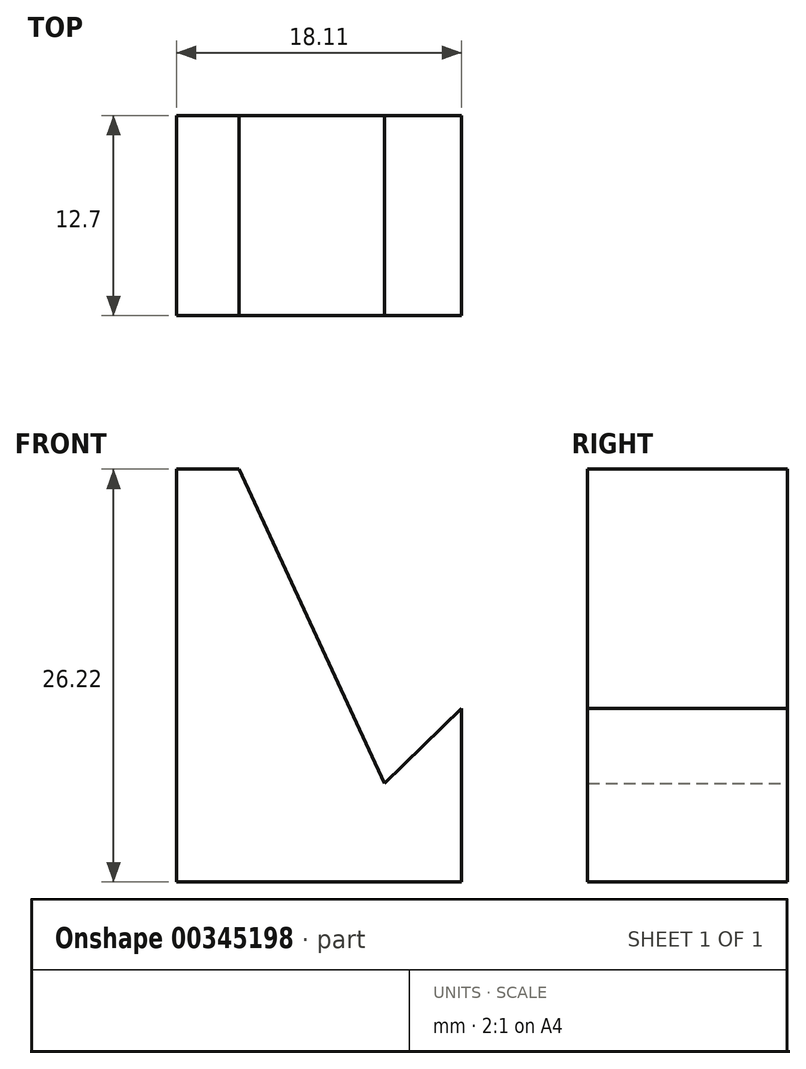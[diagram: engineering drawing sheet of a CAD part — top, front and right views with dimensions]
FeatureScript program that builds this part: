
annotation { "Feature Type Name" : "Feature", "Feature Type Description" : "" }
export const myFeature = defineFeature(function(context is Context, id is Id, definition is map)
    precondition{}
    {
        {
            var Q0;
            Q0=qCreatedBy(makeId("Front.planeOp"),FACE);
            var sketch = newSketch(context, id + "F0", { "sketchPlane" : qUnion([Q0])});
            skLineSegment(sketch, "E0", {"start": v(0, 0) * mm, "end": v(-3.97, 0) * mm});
            skLineSegment(sketch, "E1", {"start": v(-3.97, 0) * mm, "end": v(-3.97, -26.22) * mm});
            skLineSegment(sketch, "E2", {"start": v(-3.97, -26.22) * mm, "end": v(14.14, -26.22) * mm});
            skLineSegment(sketch, "E3", {"start": v(14.14, -26.22) * mm, "end": v(14.14, -15.22) * mm});
            skLineSegment(sketch, "E4", {"start": v(14.14, -15.22) * mm, "end": v(9.25, -19.96) * mm});
            skLineSegment(sketch, "E5", {"start": v(9.25, -19.96) * mm, "end": v(0, 0) * mm});
            skSolve(sketch);
        }
        {
            var Q0;
            Q0=makeQuery(id+"F0.imprint","IMPRINT",FACE,{"disambiguationData":[TD([[makeQuery(id+"F0.imprint","IMPRINT",EDGE,{"derivedFrom":sQuery(id+"F0.wireOp",EDGE,"E0")}),1.0]])]});
            extrude(context, id + "F1", {"entities" : qUnion([Q0]), "endBound" : BoundingType.SYMMETRIC, "depth" : 12.7 * mm});
        }
    });
